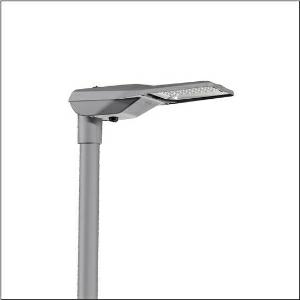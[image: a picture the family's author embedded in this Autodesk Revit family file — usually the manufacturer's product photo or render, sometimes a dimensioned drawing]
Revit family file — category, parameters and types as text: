
# Revit family: streetlight_sl_21_iq_mini___st0_5a_5xe2b31y08jb_a8c8
name_source: partatom
category: Lighting Fixtures
units: mm (PartAtom-declared; Revit-internal decimal feet)

## family parameters
Cut with Voids When Loaded = No
Host = Face
Light Source = No
Part Type = Normal
Room Calculation Point = No
Round Connector Dimension = Use Diameter
Shared = No

## types (1)
- --- (1 x LED, 11210 lm, 72.5 W, 3000K)
    Apparent Load = 73 VA
    CIE Flux Codes = 43 76 97 100 100
    Color Rendering = 70
    Color Temperature = 3000K
    Default Elevation = 1800 mm
    Description = Streetlight SL 21 iQ mini, mast luminaire, primary light control with lens, of PMMA, primary optical cover: cover, of toughened safety glass, transparent, light distribution: ST0.5a, light emission: direct distribution, primary light characteristic: asymmetric, installation type: post-top, side-entry, LED, High Power LED, rated luminous flux: 11.210lm, luminous efficacy: 155lm/W, light colour: 730, colour temperature: 3000K, control gear: iQ-Street Remote, D4i with power reduction, control: pre-setting: logarithmic dimming characteristic, Street-Remote, Auto-Match, Temp-Guard, Lumen-Switch, Night-Set, Smart-Wire, Light-Fading, Desk-Remote (wireless, voltage-free reading and setting of iQ features in the workshop via application-optimized NFC function/RFID function), optimised constant luminous flux control (CLO 2.0), mains connection: 220..240V, AC, 50/60Hz, start of lifetime: 73W, end of service life: 76W, reduction: 33W, luminaire housing, of diecast aluminium, powder-coated, Siteco® metallic grey (DB 702S), corrosivity category C5 mid according to DIN EN ISO 12944, please order mast flange separately, inclination adjustable: 0°, 5°, 10°, 15°, sealing non-destructively replaceable, multi-level sealing system, length: 628mm, width: 235mm, height: 110mm, mast flange for spigot size: 42mm (side-entry): 5XC10008XM4, 60/48mm (side-entry/post-top): 5XC10108XM2, 76/60mm (side-entry/post-top): 5XC10108XM1, mounting height: 4..8m, Smart Interface below and above, protection rating (complete): IP66, insulation class (complete): insulation class II (safety insulation), certification: CE, ENEC, ENEC+, VDE, impact resistance: IK10, permissible operating ambient temperature for outdoor applications: -40..+50°C, standard-compliant lighting for roads and squares, packaging unit: 1 piece

Light Distribution: ST0.5a
    Height = 110 mm
    Lamp = 1 x LED
    Lamp Light Flux = 11210 lm
    Lamp Power = 72.5 W
    Lamp count = 1
    Length = 625 mm
    Luminous efficacy = 155 lm/W
    Manufacturer = Siteco
    ModVariant = No
    Model = 5XE2B31Y08JB
    Number of Poles = 1
    OnlyDefault = Yes
    Power Factor = 1
    Product Name = Streetlight SL 21 iQ mini | ST0.5a
    Product group = mast luminaire | pylon top
    ProductGroupID = 6100
    Protection Class = Protection class II
    Protection Degree = IP 66
    RLX_Detail_Level = 1
    RLX_Emergency_Light_Flux = 0 lm
    RLX_Emergency_Type = 0
    RLX_Emergency_Type_DB = No
    RlxData = <blob elided: 37841 chars, md5=a2ecffba>
    Socket = socket
    Standby Power = 0 W
    System Light Flux = 11210 lm
    System Power = 73 W
    Type Comments = factory setting: luminous flux: 100 % | dim-lin: 254 | 755 mA
    Type Image = l_1003514.jpg
    URL = http://relux.com
    VarID = @adj_115836
    Voltage = 0 V
    Weight = 0.00 kg
    Width = 234 mm

## geometry (parser evidence)
native form markers: Blend x4, Sweep x13
no freeform markers — native parametric forms only
